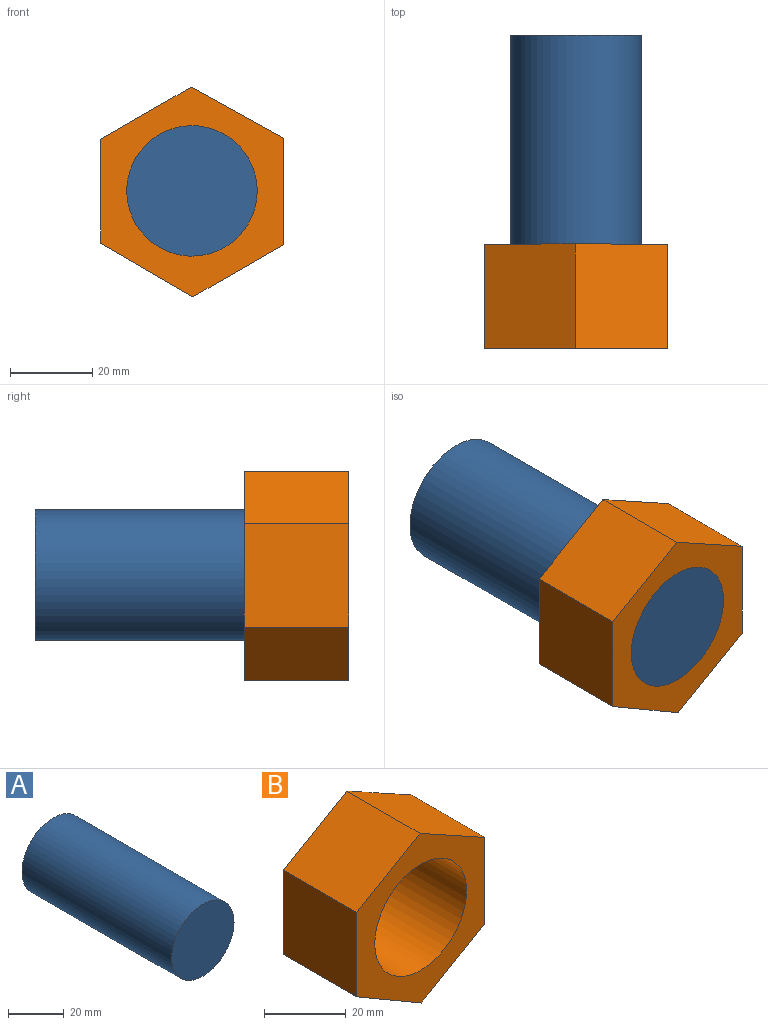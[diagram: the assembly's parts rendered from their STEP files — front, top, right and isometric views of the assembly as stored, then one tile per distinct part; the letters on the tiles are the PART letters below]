
ASSEMBLY  parts=2 mates=1
PART A: 3 faces, bbox 31.8x76.2x31.8 mm
  f0: cylinder r=15.88mm len=76.2mm, axis (0,1,0), area 7600.6mm2, adj f1,f2
  f1: plane 31.75x31.75mm, normal (0,-1,0), area 791.7mm2, adj f0
  f2: plane 31.75x31.75mm, normal (0,1,0), area 791.7mm2, adj f0
PART B: 9 faces, bbox 44.5x25.4x51.1 mm
  f0: plane 25.4x22.45mm, normal (0.48,0,0.87), area 651.9mm2, adj f1,f6,f7,f8
  f1: plane 25.4x22mm, normal (-0.5,0,0.87), area 645.2mm2, adj f0,f2,f7,f8
  f2: plane 25.4x25.27mm, normal (-1,0,0), area 641.8mm2, adj f1,f3,f7,f8
  f3: plane 25.4x22.45mm, normal (-0.5,0,-0.86), area 660.2mm2, adj f2,f4,f7,f8
  f4: plane 25.4x22mm, normal (0.5,0,-0.87), area 645.2mm2, adj f3,f6,f7,f8
  f5: cylinder r=15.88mm len=31.75mm, axis (0,1,0), area 2533.5mm2, adj f7,f8
  f6: plane 25.93x25.4mm, normal (1,0,0), area 658.5mm2, adj f0,f4,f7,f8
  f7: plane 51.06x44.45mm, normal (0,-1,0), area 912mm2, adj f0,f1,f2,f3,f4,f5,f6
  f8: plane 51.06x44.45mm, normal (0,1,0), area 912mm2, adj f0,f1,f2,f3,f4,f5,f6
PLACE A t=(-83.57,15.65,0.62)mm
PLACE B t=(-11.99,2.95,0.62)mm
MATE revolute A.f0 <-> B.f5  axis (0,-1,0) through (-11.99,-22.45,0.62)mm
